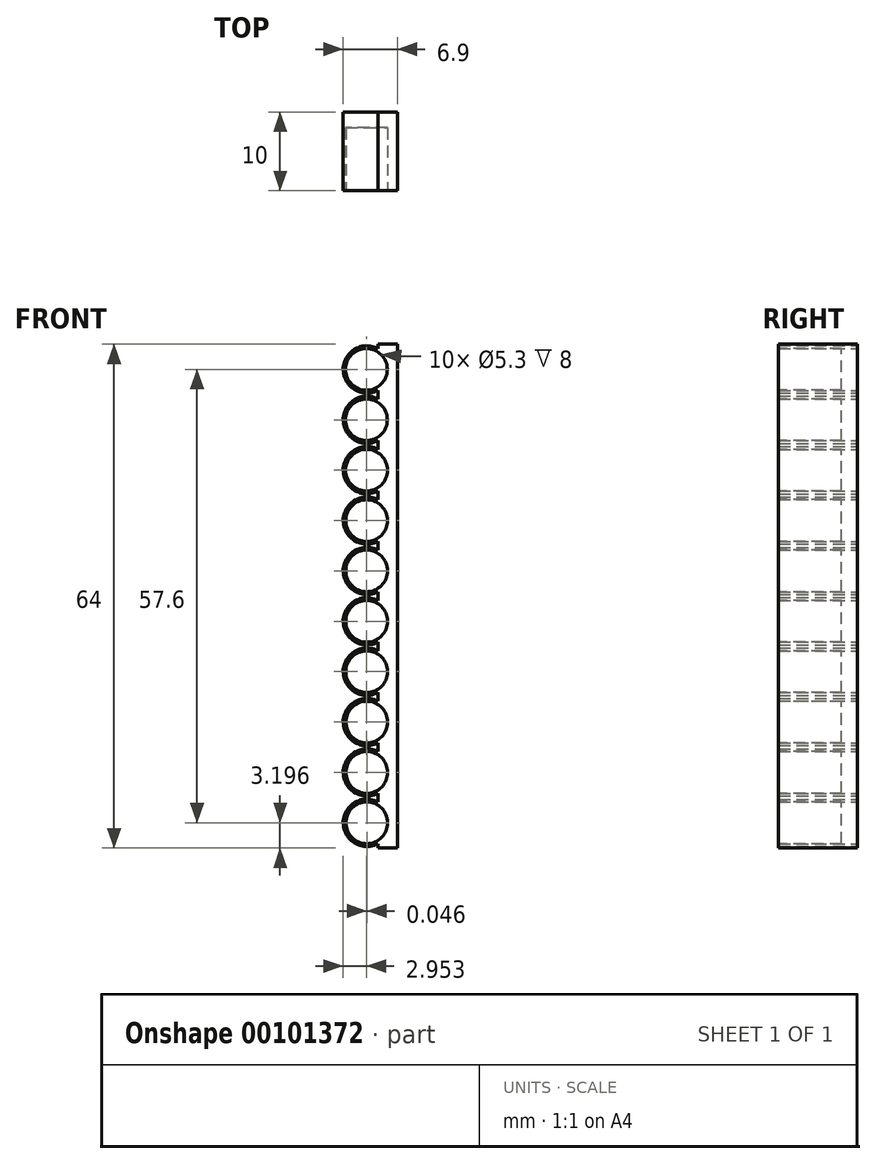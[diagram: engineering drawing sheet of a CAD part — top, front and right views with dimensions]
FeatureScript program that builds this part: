
annotation { "Feature Type Name" : "Feature", "Feature Type Description" : "" }
export const myFeature = defineFeature(function(context is Context, id is Id, definition is map)
    precondition{}
    {
        {
            var Q0;
            Q0=qCreatedBy(makeId("Front.planeOp"),FACE);
            var sketch = newSketch(context, id + "F0", { "sketchPlane" : qUnion([Q0])});
            skCircle(sketch, "E0", {"center": v(-1.28, 24.62) * mm, "radius": 3 * mm});
            skLineSegment(sketch, "E1", {"start": v(-1.28, 24.62) * mm, "end": v(-1.28, -35.95) * mm, "construction": true});
            skPoint(sketch, "E2", {"position": v(-1.28, 18.22) * mm});
            skCircle(sketch, "E3.0.1.0", {"center": v(-1.28, 18.22) * mm, "radius": 3 * mm});
            skCircle(sketch, "E3.0.2.0", {"center": v(-1.28, 11.82) * mm, "radius": 3 * mm});
            skCircle(sketch, "E3.0.3.0", {"center": v(-1.28, 5.42) * mm, "radius": 3 * mm});
            skCircle(sketch, "E3.0.4.0", {"center": v(-1.28, -0.98) * mm, "radius": 3 * mm});
            skCircle(sketch, "E3.0.5.0", {"center": v(-1.28, -7.38) * mm, "radius": 3 * mm});
            skCircle(sketch, "E3.0.6.0", {"center": v(-1.28, -13.78) * mm, "radius": 3 * mm});
            skCircle(sketch, "E3.0.7.0", {"center": v(-1.28, -20.18) * mm, "radius": 3 * mm});
            skCircle(sketch, "E3.0.8.0", {"center": v(-1.28, -26.58) * mm, "radius": 3 * mm});
            skCircle(sketch, "E3.0.9.0", {"center": v(-1.28, -32.98) * mm, "radius": 3 * mm});
            skLineSegment(sketch, "E3.direction1", {"start": v(-1.28, 24.62) * mm, "end": v(23.67, 24.62) * mm, "construction": true});
            skLineSegment(sketch, "E3.direction2", {"start": v(-1.28, 24.62) * mm, "end": v(-1.28, 18.22) * mm, "construction": true});
            skLineSegment(sketch, "E4.bottom", {"start": v(2.62, 27.82) * mm, "end": v(0.12, 27.82) * mm});
            skLineSegment(sketch, "E4.top", {"start": v(2.62, -36.18) * mm, "end": v(0.12, -36.18) * mm});
            skLineSegment(sketch, "E4.left", {"start": v(2.62, 27.82) * mm, "end": v(2.62, -36.18) * mm});
            skLineSegment(sketch, "E4.right", {"start": v(0.12, 27.82) * mm, "end": v(0.12, -36.18) * mm});
            skSolve(sketch);
        }
        {
            var Q0;
            {var subQ0=sQuery(id+"F0.wireOp",EDGE,"E4.right");var subQ1=sQuery(id+"F0.wireOp",EDGE,"E3.0.9.0");var subQ2=makeQuery(id+"F0.imprint","INTERSECT",VERTEX,{"disambiguationData":[OD(0.0)],"derivedFrom":[subQ1,subQ0]});Q0=makeQuery(id+"F0.imprint","IMPRINT",FACE,{"disambiguationData":[TD([[makeQuery(id+"F0.imprint","IMPRINT",EDGE,{"disambiguationData":[TD([[subQ2,1.0]])],"derivedFrom":subQ1}),1.0]])]});}
            var Q1;
            {var subQ0=sQuery(id+"F0.wireOp",EDGE,"E4.right");var subQ1=sQuery(id+"F0.wireOp",EDGE,"E3.0.7.0");var subQ2=makeQuery(id+"F0.imprint","INTERSECT",VERTEX,{"disambiguationData":[OD(0.0)],"derivedFrom":[subQ1,subQ0]});Q1=makeQuery(id+"F0.imprint","IMPRINT",FACE,{"disambiguationData":[TD([[makeQuery(id+"F0.imprint","IMPRINT",EDGE,{"disambiguationData":[TD([[subQ2,1.0]])],"derivedFrom":subQ1}),1.0]])]});}
            var Q2;
            {var subQ26=sQuery(id+"F0.wireOp",EDGE,"E4.bottom");Q2=makeQuery(id+"F0.imprint","IMPRINT",FACE,{"disambiguationData":[TD([[makeQuery(id+"F0.imprint","IMPRINT",EDGE,{"derivedFrom":subQ26}),1.0]])]});}
            var Q3;
            {var subQ0=sQuery(id+"F0.wireOp",EDGE,"E4.right");var subQ1=sQuery(id+"F0.wireOp",EDGE,"E3.0.5.0");var subQ2=makeQuery(id+"F0.imprint","INTERSECT",VERTEX,{"disambiguationData":[OD(0.0)],"derivedFrom":[subQ1,subQ0]});Q3=makeQuery(id+"F0.imprint","IMPRINT",FACE,{"disambiguationData":[TD([[makeQuery(id+"F0.imprint","IMPRINT",EDGE,{"disambiguationData":[TD([[subQ2,1.0]])],"derivedFrom":subQ1}),1.0]])]});}
            var Q4;
            {var subQ0=sQuery(id+"F0.wireOp",EDGE,"E4.right");var subQ1=sQuery(id+"F0.wireOp",EDGE,"E3.0.8.0");var subQ2=makeQuery(id+"F0.imprint","INTERSECT",VERTEX,{"disambiguationData":[OD(0.0)],"derivedFrom":[subQ1,subQ0]});Q4=makeQuery(id+"F0.imprint","IMPRINT",FACE,{"disambiguationData":[TD([[makeQuery(id+"F0.imprint","IMPRINT",EDGE,{"disambiguationData":[TD([[subQ2,1.0]])],"derivedFrom":subQ1}),1.0]])]});}
            var Q5;
            {var subQ0=sQuery(id+"F0.wireOp",EDGE,"E4.right");var subQ1=sQuery(id+"F0.wireOp",EDGE,"E3.0.3.0");var subQ2=makeQuery(id+"F0.imprint","INTERSECT",VERTEX,{"disambiguationData":[OD(0.0)],"derivedFrom":[subQ1,subQ0]});Q5=makeQuery(id+"F0.imprint","IMPRINT",FACE,{"disambiguationData":[TD([[makeQuery(id+"F0.imprint","IMPRINT",EDGE,{"disambiguationData":[TD([[subQ2,1.0]])],"derivedFrom":subQ1}),1.0]])]});}
            var Q6;
            {var subQ0=sQuery(id+"F0.wireOp",EDGE,"E4.right");var subQ1=sQuery(id+"F0.wireOp",EDGE,"E3.0.6.0");var subQ2=makeQuery(id+"F0.imprint","INTERSECT",VERTEX,{"disambiguationData":[OD(0.0)],"derivedFrom":[subQ1,subQ0]});Q6=makeQuery(id+"F0.imprint","IMPRINT",FACE,{"disambiguationData":[TD([[makeQuery(id+"F0.imprint","IMPRINT",EDGE,{"disambiguationData":[TD([[subQ2,1.0]])],"derivedFrom":subQ1}),1.0]])]});}
            var Q7;
            {var subQ0=sQuery(id+"F0.wireOp",EDGE,"E4.right");var subQ1=sQuery(id+"F0.wireOp",EDGE,"E3.0.4.0");var subQ2=makeQuery(id+"F0.imprint","INTERSECT",VERTEX,{"disambiguationData":[OD(0.0)],"derivedFrom":[subQ1,subQ0]});Q7=makeQuery(id+"F0.imprint","IMPRINT",FACE,{"disambiguationData":[TD([[makeQuery(id+"F0.imprint","IMPRINT",EDGE,{"disambiguationData":[TD([[subQ2,1.0]])],"derivedFrom":subQ1}),1.0]])]});}
            var Q8;
            {var subQ0=sQuery(id+"F0.wireOp",EDGE,"E4.right");var subQ1=sQuery(id+"F0.wireOp",EDGE,"E0");var subQ2=makeQuery(id+"F0.imprint","INTERSECT",VERTEX,{"disambiguationData":[OD(0.0)],"derivedFrom":[subQ1,subQ0]});Q8=makeQuery(id+"F0.imprint","IMPRINT",FACE,{"disambiguationData":[TD([[makeQuery(id+"F0.imprint","IMPRINT",EDGE,{"disambiguationData":[TD([[subQ2,-1.0]])],"derivedFrom":subQ1}),1.0]])]});}
            var Q9;
            {var subQ0=sQuery(id+"F0.wireOp",EDGE,"E4.right");var subQ1=sQuery(id+"F0.wireOp",EDGE,"E3.0.1.0");var subQ2=makeQuery(id+"F0.imprint","INTERSECT",VERTEX,{"disambiguationData":[OD(0.0)],"derivedFrom":[subQ1,subQ0]});Q9=makeQuery(id+"F0.imprint","IMPRINT",FACE,{"disambiguationData":[TD([[makeQuery(id+"F0.imprint","IMPRINT",EDGE,{"disambiguationData":[TD([[subQ2,-1.0]])],"derivedFrom":subQ1}),1.0]])]});}
            var Q10;
            {var subQ0=sQuery(id+"F0.wireOp",EDGE,"E4.right");var subQ1=sQuery(id+"F0.wireOp",EDGE,"E3.0.2.0");var subQ2=makeQuery(id+"F0.imprint","INTERSECT",VERTEX,{"disambiguationData":[OD(0.0)],"derivedFrom":[subQ1,subQ0]});Q10=makeQuery(id+"F0.imprint","IMPRINT",FACE,{"disambiguationData":[TD([[makeQuery(id+"F0.imprint","IMPRINT",EDGE,{"disambiguationData":[TD([[subQ2,-1.0]])],"derivedFrom":subQ1}),1.0]])]});}
            var Q11;
            {var subQ0=sQuery(id+"F0.wireOp",EDGE,"E4.right");var subQ1=sQuery(id+"F0.wireOp",EDGE,"E3.0.3.0");var subQ2=makeQuery(id+"F0.imprint","INTERSECT",VERTEX,{"disambiguationData":[OD(0.0)],"derivedFrom":[subQ1,subQ0]});Q11=makeQuery(id+"F0.imprint","IMPRINT",FACE,{"disambiguationData":[TD([[makeQuery(id+"F0.imprint","IMPRINT",EDGE,{"disambiguationData":[TD([[subQ2,-1.0]])],"derivedFrom":subQ1}),1.0]])]});}
            var Q12;
            {var subQ0=sQuery(id+"F0.wireOp",EDGE,"E4.right");var subQ1=sQuery(id+"F0.wireOp",EDGE,"E3.0.4.0");var subQ2=makeQuery(id+"F0.imprint","INTERSECT",VERTEX,{"disambiguationData":[OD(0.0)],"derivedFrom":[subQ1,subQ0]});Q12=makeQuery(id+"F0.imprint","IMPRINT",FACE,{"disambiguationData":[TD([[makeQuery(id+"F0.imprint","IMPRINT",EDGE,{"disambiguationData":[TD([[subQ2,-1.0]])],"derivedFrom":subQ1}),1.0]])]});}
            var Q13;
            {var subQ0=sQuery(id+"F0.wireOp",EDGE,"E4.right");var subQ1=sQuery(id+"F0.wireOp",EDGE,"E3.0.5.0");var subQ2=makeQuery(id+"F0.imprint","INTERSECT",VERTEX,{"disambiguationData":[OD(0.0)],"derivedFrom":[subQ1,subQ0]});Q13=makeQuery(id+"F0.imprint","IMPRINT",FACE,{"disambiguationData":[TD([[makeQuery(id+"F0.imprint","IMPRINT",EDGE,{"disambiguationData":[TD([[subQ2,-1.0]])],"derivedFrom":subQ1}),1.0]])]});}
            var Q14;
            {var subQ0=sQuery(id+"F0.wireOp",EDGE,"E4.right");var subQ1=sQuery(id+"F0.wireOp",EDGE,"E3.0.6.0");var subQ2=makeQuery(id+"F0.imprint","INTERSECT",VERTEX,{"disambiguationData":[OD(0.0)],"derivedFrom":[subQ1,subQ0]});Q14=makeQuery(id+"F0.imprint","IMPRINT",FACE,{"disambiguationData":[TD([[makeQuery(id+"F0.imprint","IMPRINT",EDGE,{"disambiguationData":[TD([[subQ2,-1.0]])],"derivedFrom":subQ1}),1.0]])]});}
            var Q15;
            {var subQ0=sQuery(id+"F0.wireOp",EDGE,"E4.right");var subQ1=sQuery(id+"F0.wireOp",EDGE,"E3.0.7.0");var subQ2=makeQuery(id+"F0.imprint","INTERSECT",VERTEX,{"disambiguationData":[OD(0.0)],"derivedFrom":[subQ1,subQ0]});Q15=makeQuery(id+"F0.imprint","IMPRINT",FACE,{"disambiguationData":[TD([[makeQuery(id+"F0.imprint","IMPRINT",EDGE,{"disambiguationData":[TD([[subQ2,-1.0]])],"derivedFrom":subQ1}),1.0]])]});}
            var Q16;
            {var subQ0=sQuery(id+"F0.wireOp",EDGE,"E4.right");var subQ1=sQuery(id+"F0.wireOp",EDGE,"E3.0.8.0");var subQ2=makeQuery(id+"F0.imprint","INTERSECT",VERTEX,{"disambiguationData":[OD(0.0)],"derivedFrom":[subQ1,subQ0]});Q16=makeQuery(id+"F0.imprint","IMPRINT",FACE,{"disambiguationData":[TD([[makeQuery(id+"F0.imprint","IMPRINT",EDGE,{"disambiguationData":[TD([[subQ2,-1.0]])],"derivedFrom":subQ1}),1.0]])]});}
            var Q17;
            {var subQ0=sQuery(id+"F0.wireOp",EDGE,"E4.right");var subQ1=sQuery(id+"F0.wireOp",EDGE,"E3.0.9.0");var subQ2=makeQuery(id+"F0.imprint","INTERSECT",VERTEX,{"disambiguationData":[OD(0.0)],"derivedFrom":[subQ1,subQ0]});Q17=makeQuery(id+"F0.imprint","IMPRINT",FACE,{"disambiguationData":[TD([[makeQuery(id+"F0.imprint","IMPRINT",EDGE,{"disambiguationData":[TD([[subQ2,-1.0]])],"derivedFrom":subQ1}),1.0]])]});}
            var Q18;
            {var subQ0=sQuery(id+"F0.wireOp",EDGE,"E4.right");var subQ1=sQuery(id+"F0.wireOp",EDGE,"E0");var subQ2=makeQuery(id+"F0.imprint","INTERSECT",VERTEX,{"disambiguationData":[OD(0.0)],"derivedFrom":[subQ1,subQ0]});Q18=makeQuery(id+"F0.imprint","IMPRINT",FACE,{"disambiguationData":[TD([[makeQuery(id+"F0.imprint","IMPRINT",EDGE,{"disambiguationData":[TD([[subQ2,1.0]])],"derivedFrom":subQ1}),1.0]])]});}
            var Q19;
            {var subQ0=sQuery(id+"F0.wireOp",EDGE,"E4.right");var subQ1=sQuery(id+"F0.wireOp",EDGE,"E3.0.1.0");var subQ2=makeQuery(id+"F0.imprint","INTERSECT",VERTEX,{"disambiguationData":[OD(0.0)],"derivedFrom":[subQ1,subQ0]});Q19=makeQuery(id+"F0.imprint","IMPRINT",FACE,{"disambiguationData":[TD([[makeQuery(id+"F0.imprint","IMPRINT",EDGE,{"disambiguationData":[TD([[subQ2,1.0]])],"derivedFrom":subQ1}),1.0]])]});}
            var Q20;
            {var subQ0=sQuery(id+"F0.wireOp",EDGE,"E4.right");var subQ1=sQuery(id+"F0.wireOp",EDGE,"E3.0.2.0");var subQ2=makeQuery(id+"F0.imprint","INTERSECT",VERTEX,{"disambiguationData":[OD(0.0)],"derivedFrom":[subQ1,subQ0]});Q20=makeQuery(id+"F0.imprint","IMPRINT",FACE,{"disambiguationData":[TD([[makeQuery(id+"F0.imprint","IMPRINT",EDGE,{"disambiguationData":[TD([[subQ2,1.0]])],"derivedFrom":subQ1}),1.0]])]});}
            extrude(context, id + "F1", {"entities" : qUnion([Q0, Q1, Q2, Q3, Q4, Q5, Q6, Q7, Q8, Q9, Q10, Q11, Q12, Q13, Q14, Q15, Q16, Q17, Q18, Q19, Q20]), "depth" : 10 * mm});
        }
        {
            var Q0;
            Q0=makeQuery(id+"F1.opExtrude","CAP_FACE",FACE,{"disambiguationData":[OSD([sQuery(id+"F0.wireOp",EDGE,"E0"),sQuery(id+"F0.wireOp",EDGE,"E3.0.1.0"),sQuery(id+"F0.wireOp",EDGE,"E3.0.2.0"),sQuery(id+"F0.wireOp",EDGE,"E3.0.3.0"),sQuery(id+"F0.wireOp",EDGE,"E3.0.4.0"),sQuery(id+"F0.wireOp",EDGE,"E3.0.5.0"),sQuery(id+"F0.wireOp",EDGE,"E3.0.6.0"),sQuery(id+"F0.wireOp",EDGE,"E3.0.7.0"),sQuery(id+"F0.wireOp",EDGE,"E3.0.8.0"),sQuery(id+"F0.wireOp",EDGE,"E3.0.9.0"),sQuery(id+"F0.wireOp",EDGE,"E4.bottom"),sQuery(id+"F0.wireOp",EDGE,"E4.top"),sQuery(id+"F0.wireOp",EDGE,"E4.left"),sQuery(id+"F0.wireOp",EDGE,"E4.right")])],"isStart":false});
            var sketch = newSketch(context, id + "F2", { "sketchPlane" : qUnion([Q0])});
            skCircle(sketch, "E5", {"center": v(-1.28, -32.98) * mm, "radius": 2.65 * mm});
            skCircle(sketch, "E6.1.0.0", {"center": v(-1.29, -26.58) * mm, "radius": 2.65 * mm});
            skCircle(sketch, "E6.2.0.0", {"center": v(-1.3, -20.18) * mm, "radius": 2.65 * mm});
            skCircle(sketch, "E6.3.0.0", {"center": v(-1.3, -13.78) * mm, "radius": 2.65 * mm});
            skCircle(sketch, "E6.4.0.0", {"center": v(-1.3, -7.38) * mm, "radius": 2.65 * mm});
            skCircle(sketch, "E6.5.0.0", {"center": v(-1.3, -0.98) * mm, "radius": 2.65 * mm});
            skCircle(sketch, "E6.6.0.0", {"center": v(-1.31, 5.42) * mm, "radius": 2.65 * mm});
            skCircle(sketch, "E6.7.0.0", {"center": v(-1.32, 11.82) * mm, "radius": 2.65 * mm});
            skCircle(sketch, "E6.8.0.0", {"center": v(-1.32, 18.22) * mm, "radius": 2.65 * mm});
            skCircle(sketch, "E6.9.0.0", {"center": v(-1.33, 24.62) * mm, "radius": 2.65 * mm});
            skLineSegment(sketch, "E6.direction1", {"start": v(-1.28, -32.98) * mm, "end": v(-1.29, -26.58) * mm, "construction": true});
            skSolve(sketch);
        }
        {
            var Q0;
            Q0 = qSketchRegion(id + "F2", true);
            extrude(context, id + "F3", {"entities" : qUnion([Q0]), "operationType" : NewBodyOperationType.REMOVE, "oppositeDirection" : true, "depth" : 8 * mm});
        }
    });
